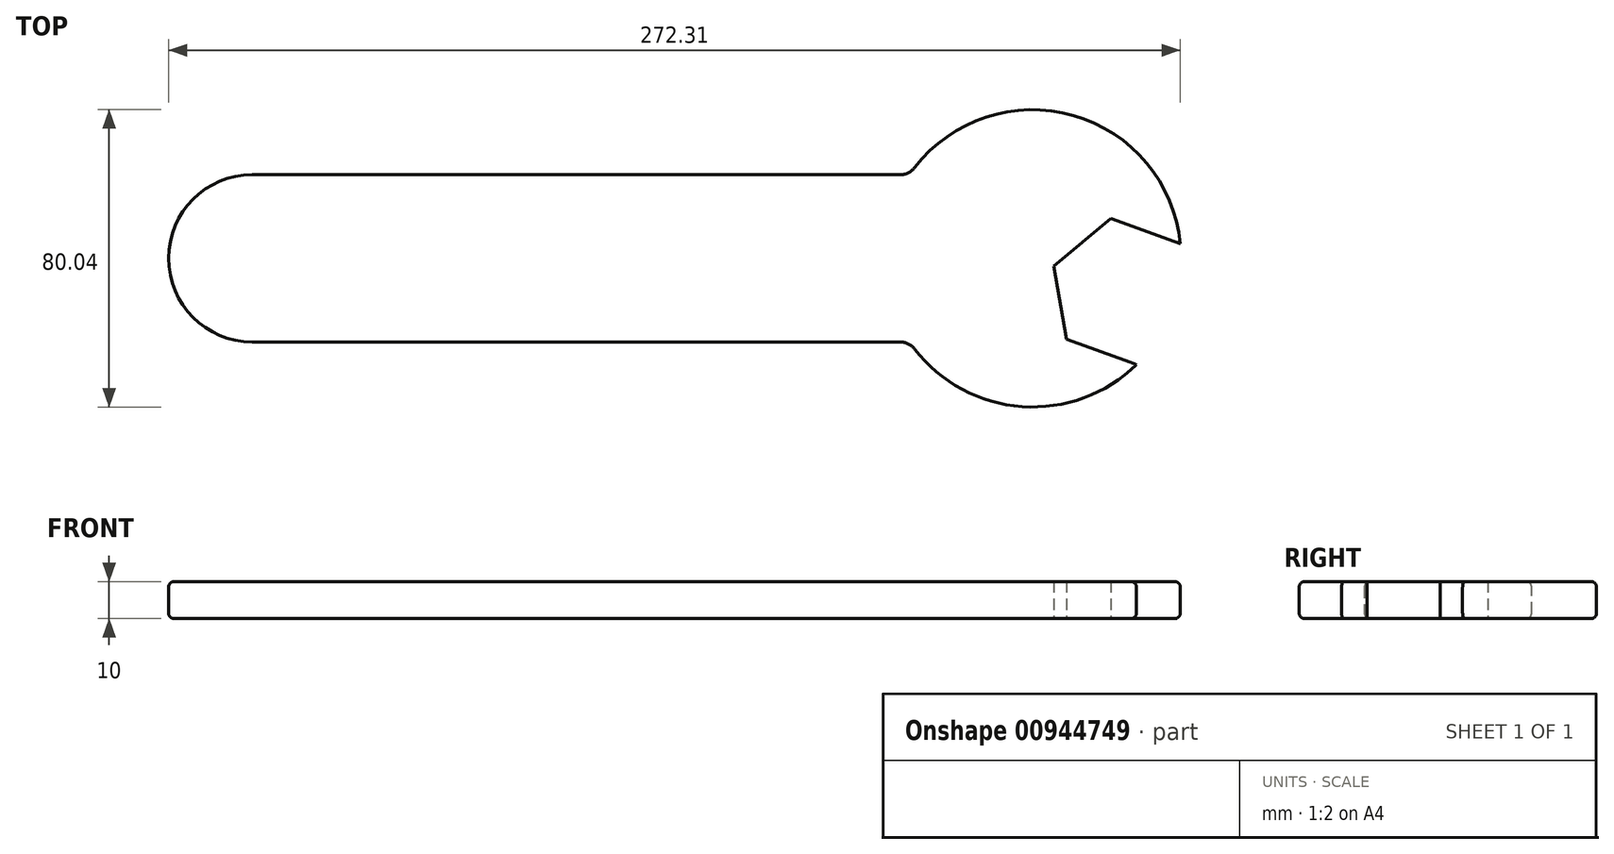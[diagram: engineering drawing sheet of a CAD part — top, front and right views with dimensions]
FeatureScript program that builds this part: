
annotation { "Feature Type Name" : "Feature", "Feature Type Description" : "" }
export const myFeature = defineFeature(function(context is Context, id is Id, definition is map)
    precondition{}
    {
        {
            var Q0;
            Q0=qCreatedBy(makeId("Top.planeOp"),FACE);
            var sketch = newSketch(context, id + "F0", { "sketchPlane" : qUnion([Q0])});
            skLineSegment(sketch, "E0.bottom", {"start": v(-90, 22.5) * mm, "end": v(90, 22.5) * mm, "construction": true});
            skLineSegment(sketch, "E0.top", {"start": v(-90, -22.5) * mm, "end": v(90, -22.5) * mm, "construction": true});
            skLineSegment(sketch, "E0.left", {"start": v(-90, 22.5) * mm, "end": v(-90, -22.5) * mm, "construction": true});
            skLineSegment(sketch, "E0.right", {"start": v(90, 22.5) * mm, "end": v(90, -22.5) * mm, "construction": true});
            skPoint(sketch, "E0.middle", {"position": v(0, 0) * mm});
            skPoint(sketch, "E1", {"position": v(-90, 0) * mm});
            skArc(sketch, "E2", {"start": v(-90, 22.5) * mm, "mid": v(-112.5, 0) * mm, "end": v(-90, -22.5) * mm});
            skCircle(sketch, "E3", {"center": v(120, 0) * mm, "radius": 40 * mm, "construction": true});
            skPoint(sketch, "E3.centerSnap0", {"position": v(90, 0) * mm});
            skLineSegment(sketch, "E4", {"start": v(130, 0) * mm, "end": v(217.79, 0) * mm, "construction": true});
            skLineSegment(sketch, "E5", {"start": v(120, 0) * mm, "end": v(194.46, -27.1) * mm, "construction": true});
            skLineSegment(sketch, "E6", {"start": v(219.24, 70.29) * mm, "end": v(239.19, 71.76) * mm});
            skLineSegment(sketch, "E7", {"start": v(239.19, 71.76) * mm, "end": v(250.44, 55.22) * mm});
            skLineSegment(sketch, "E8", {"start": v(250.44, 55.22) * mm, "end": v(241.74, 37.21) * mm});
            skLineSegment(sketch, "E9", {"start": v(241.74, 37.21) * mm, "end": v(221.8, 35.74) * mm});
            skLineSegment(sketch, "E10", {"start": v(221.8, 35.74) * mm, "end": v(210.55, 52.28) * mm});
            skLineSegment(sketch, "E11", {"start": v(210.55, 52.28) * mm, "end": v(219.24, 70.29) * mm});
            skLineSegment(sketch, "E12", {"start": v(210.55, 52.28) * mm, "end": v(250.44, 55.22) * mm});
            skLineSegment(sketch, "E13", {"start": v(229.22, 71.02) * mm, "end": v(231.77, 36.48) * mm});
            skLineSegment(sketch, "E14", {"start": v(157.59, -13.68) * mm, "end": v(125.73, -2.09) * mm});
            skLineSegment(sketch, "E15", {"start": v(125.73, -2.09) * mm, "end": v(141.05, 10.77) * mm});
            skLineSegment(sketch, "E16", {"start": v(141.05, 10.77) * mm, "end": v(159.85, 3.93) * mm});
            skLineSegment(sketch, "E17", {"start": v(125.73, -2.09) * mm, "end": v(129.2, -21.78) * mm});
            skLineSegment(sketch, "E18", {"start": v(129.2, -21.78) * mm, "end": v(148, -28.62) * mm});
            skPoint(sketch, "E19", {"position": v(-90, 22.5) * mm});
            skPoint(sketch, "E20", {"position": v(-90, -22.5) * mm});
            skPoint(sketch, "E21", {"position": v(90, -22.5) * mm});
            skPoint(sketch, "E22", {"position": v(90, 22.5) * mm});
            skPoint(sketch, "E23", {"position": v(86.93, 22.5) * mm});
            skPoint(sketch, "E24", {"position": v(86.93, -22.5) * mm});
            skPoint(sketch, "E25", {"position": v(125.73, -2.09) * mm});
            skPoint(sketch, "E26", {"position": v(141.05, 10.77) * mm});
            skPoint(sketch, "E27", {"position": v(159.85, 3.93) * mm});
            skPoint(sketch, "E28", {"position": v(129.2, -21.78) * mm});
            skPoint(sketch, "E29", {"position": v(148, -28.62) * mm});
            skLineSegment(sketch, "E30", {"start": v(-90, -22.5) * mm, "end": v(86.93, -22.5) * mm});
            skLineSegment(sketch, "E31", {"start": v(86.93, 22.5) * mm, "end": v(-90, 22.5) * mm});
            skArc(sketch, "E32", {"start": v(86.93, 22.5) * mm, "mid": v(129.87, 38.76) * mm, "end": v(159.8, 3.94) * mm});
            skArc(sketch, "E33", {"start": v(148, -28.62) * mm, "mid": v(116, -39.84) * mm, "end": v(86.88, -22.5) * mm});
            skSolve(sketch);
        }
        {
            var Q0;
            {var subQ3=sQuery(id+"F0.wireOp",EDGE,"E2");Q0=makeQuery(id+"F0.imprint","IMPRINT",FACE,{"disambiguationData":[TD([[makeQuery(id+"F0.imprint","IMPRINT",EDGE,{"derivedFrom":subQ3}),1.0]])]});}
            extrude(context, id + "F1", {"entities" : qUnion([Q0]), "depth" : 10 * mm, "offsetDistance" : 25 * mm});
        }
        {
            var Q0;
            Q0=makeQuery(id+"F1.opExtrude","SWEPT_EDGE",EDGE,{"disambiguationData":[OSD([sQuery(id+"F0.wireOp",EDGE,"E31"),sQuery(id+"F0.wireOp",EDGE,"E32")])]});
            var Q1;
            Q1=makeQuery(id+"F1.opExtrude","SWEPT_EDGE",EDGE,{"disambiguationData":[OSD([sQuery(id+"F0.wireOp",EDGE,"E30"),sQuery(id+"F0.wireOp",EDGE,"E33")])]});
            fillet(context, id + "F2", {"entities" : qUnion([Q0, Q1]), "radius" : 5 * mm, "tangentPropagation" : true, "allowEdgeOverflow" : false});
        }
        {
            var Q0;
            Q0=makeQuery(id+"F1.opExtrude","CAP_EDGE",EDGE,{"disambiguationData":[OSD([sQuery(id+"F0.wireOp",EDGE,"E31")])],"isStart":false});
            var Q1;
            Q1=makeQuery(id+"F1.opExtrude","CAP_EDGE",EDGE,{"disambiguationData":[OSD([sQuery(id+"F0.wireOp",EDGE,"E30")])],"isStart":true});
            fillet(context, id + "F3", {"entities" : qUnion([Q0, Q1]), "radius" : 1.5 * mm, "tangentPropagation" : true, "allowEdgeOverflow" : false});
        }
    });
